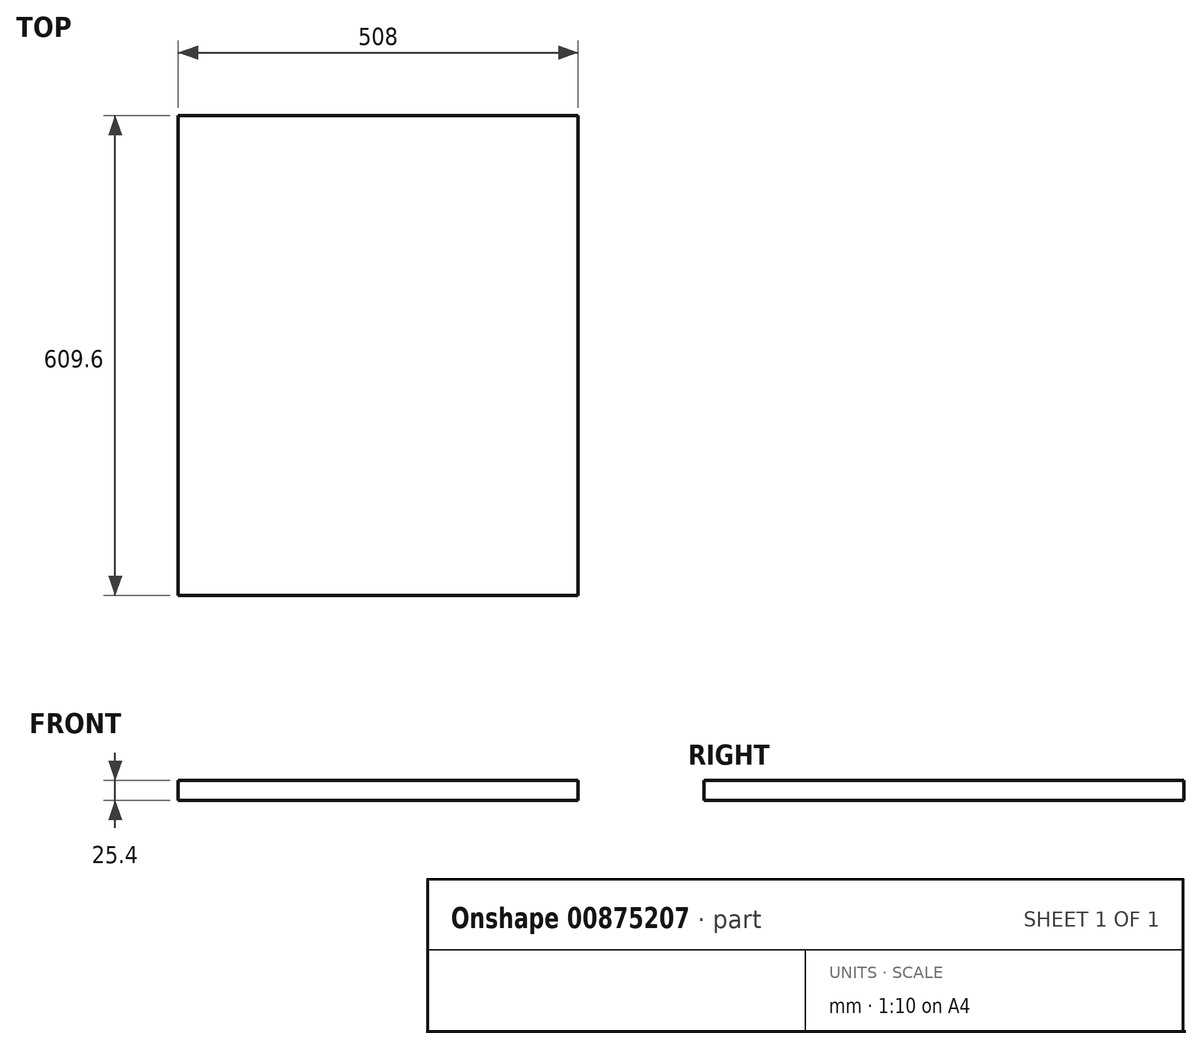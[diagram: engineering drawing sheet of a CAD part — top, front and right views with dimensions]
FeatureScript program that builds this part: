
annotation { "Feature Type Name" : "Feature", "Feature Type Description" : "" }
export const myFeature = defineFeature(function(context is Context, id is Id, definition is map)
    precondition{}
    {
        {
            var Q0;
            Q0=qCreatedBy(makeId("Top.planeOp"),FACE);
            var sketch = newSketch(context, id + "F0", { "sketchPlane" : qUnion([Q0])});
            skLineSegment(sketch, "E0.bottom", {"start": v(-254, 304.8) * mm, "end": v(254, 304.8) * mm});
            skLineSegment(sketch, "E0.top", {"start": v(-254, -304.8) * mm, "end": v(254, -304.8) * mm});
            skLineSegment(sketch, "E0.left", {"start": v(-254, 304.8) * mm, "end": v(-254, -304.8) * mm});
            skLineSegment(sketch, "E0.right", {"start": v(254, 304.8) * mm, "end": v(254, -304.8) * mm});
            skPoint(sketch, "E0.middle", {"position": v(0, 0) * mm});
            skSolve(sketch);
        }
        {
            var Q0;
            Q0=makeQuery(id+"F0.imprint","IMPRINT",FACE,{"disambiguationData":[TD([[makeQuery(id+"F0.imprint","IMPRINT",EDGE,{"derivedFrom":sQuery(id+"F0.wireOp",EDGE,"E0.bottom")}),-1.0]])]});
            extrude(context, id + "F1", {"entities" : qUnion([Q0]), "depth" : 25.4 * mm, "offsetDistance" : 25.4 * mm});
        }
    });
